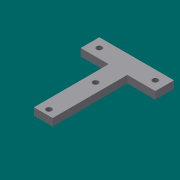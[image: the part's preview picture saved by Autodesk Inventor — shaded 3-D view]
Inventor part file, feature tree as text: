
AUTODESK INVENTOR PART (.ipt)
format: ipt  version: 2013 (Build 170138000, 138)  size: 87,040 bytes
history: native  units: mm
features: other x1, extrude x1, sketch x1
ambient origin geometry x8: Origin, YZ Plane, XZ Plane, XY Plane, X Axis, Y Axis, Z Axis, Center Point
feature tree (3):
  other  "ソリッド1"
  extrude  "押し出し1"  Depth=10.0mm
  sketch  "スケッチ1"
